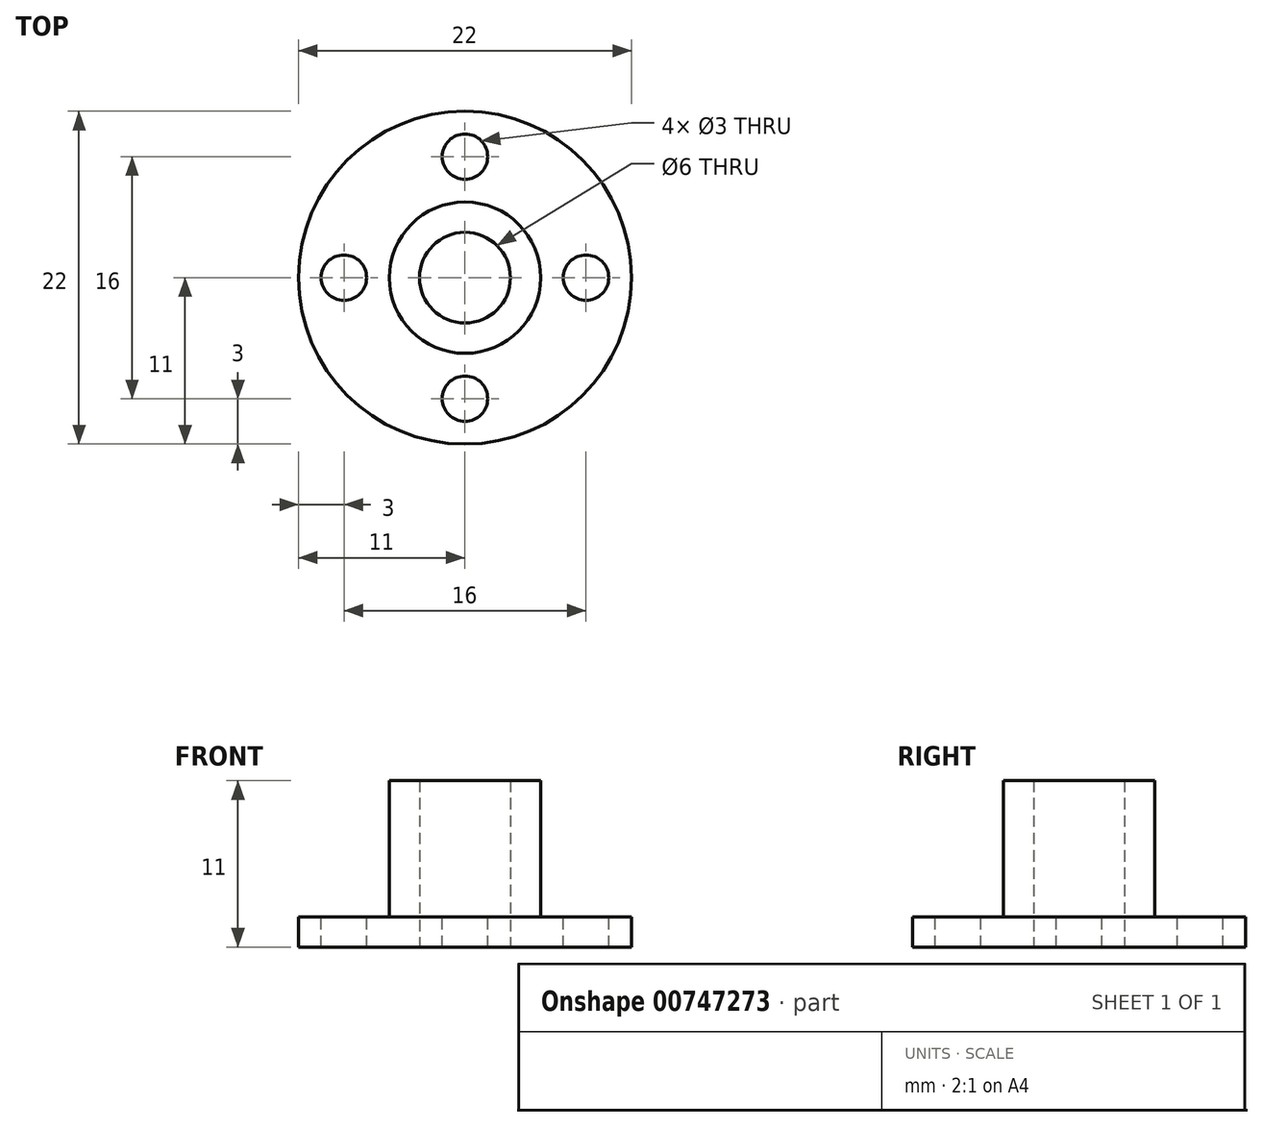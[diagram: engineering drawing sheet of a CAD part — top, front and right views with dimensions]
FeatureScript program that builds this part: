
annotation { "Feature Type Name" : "Feature", "Feature Type Description" : "" }
export const myFeature = defineFeature(function(context is Context, id is Id, definition is map)
    precondition{}
    {
        {
            var Q0;
            Q0=qCreatedBy(makeId("Top.planeOp"),FACE);
            var sketch = newSketch(context, id + "F0", { "sketchPlane" : qUnion([Q0])});
            skCircle(sketch, "E0", {"center": v(0, 0) * mm, "radius": 11 * mm});
            skSolve(sketch);
        }
        {
            var Q0;
            Q0=qSketchRegion(id+"F0",true);
            extrude(context, id + "F1", {"entities" : qUnion([Q0]), "depth" : 2 * mm, "offsetDistance" : 25 * mm});
        }
        {
            var Q0;
            Q0=makeQuery(id+"F1.opExtrude","CAP_FACE",FACE,{"disambiguationData":[OSD([sQuery(id+"F0.wireOp",EDGE,"E0")])],"isStart":false});
            var sketch = newSketch(context, id + "F2", { "sketchPlane" : qUnion([Q0])});
            skCircle(sketch, "E1", {"center": v(0, 0) * mm, "radius": 5 * mm});
            skCircle(sketch, "E2", {"center": v(0, 0) * mm, "radius": 3 * mm});
            skSolve(sketch);
        }
        {
            var Q0;
            Q0=makeQuery(id+"F2.imprint","IMPRINT",FACE,{"disambiguationData":[TD([[makeQuery(id+"F2.imprint","IMPRINT",EDGE,{"derivedFrom":sQuery(id+"F2.wireOp",EDGE,"E1")}),1.0]])]});
            extrude(context, id + "F3", {"entities" : qUnion([Q0]), "operationType" : NewBodyOperationType.ADD, "depth" : 9 * mm, "offsetDistance" : 25 * mm});
        }
        {
            var Q0;
            Q0=makeQuery(id+"F3.boolean.opBoolean","SPLIT",FACE,{"disambiguationData":[TD([makeQuery(id+"F3.opExtrude","SWEPT_FACE",FACE,{"disambiguationData":[OSD([sQuery(id+"F2.wireOp",EDGE,"E2")])]})])],"derivedFrom":makeQuery(id+"F1.opExtrude","CAP_FACE",FACE,{"disambiguationData":[OSD([sQuery(id+"F0.wireOp",EDGE,"E0")])],"isStart":false})});
            var sketch = newSketch(context, id + "F4", { "sketchPlane" : qUnion([Q0])});
            skCircle(sketch, "E3", {"center": v(0, 0) * mm, "radius": 3 * mm});
            skSolve(sketch);
        }
        {
            var Q0;
            Q0=qSketchRegion(id+"F4",true);
            var Q1;
            Q1=makeQuery(id+"F1.opExtrude","CAP_FACE",FACE,{"disambiguationData":[OSD([sQuery(id+"F0.wireOp",EDGE,"E0")])],"isStart":true});
            extrude(context, id + "F5", {"entities" : qUnion([Q0]), "operationType" : NewBodyOperationType.REMOVE, "endBound" : BoundingType.UP_TO_SURFACE, "oppositeDirection" : true, "depth" : 25 * mm, "endBoundEntityFace" : qUnion([Q1]), "offsetDistance" : 25 * mm});
        }
        {
            var Q0;
            {var subQ0=sQuery(id+"F0.wireOp",EDGE,"E0");Q0=makeQuery(id+"F3.boolean.opBoolean","SPLIT",FACE,{"disambiguationData":[TD([makeQuery(id+"F1.opExtrude","SWEPT_FACE",FACE,{"disambiguationData":[OSD([subQ0])]})])],"derivedFrom":makeQuery(id+"F1.opExtrude","CAP_FACE",FACE,{"disambiguationData":[OSD([subQ0])],"isStart":false})});}
            var sketch = newSketch(context, id + "F6", { "sketchPlane" : qUnion([Q0])});
            skCircle(sketch, "E4", {"center": v(0, 0) * mm, "radius": 8 * mm, "construction": true});
            skLineSegment(sketch, "E5", {"start": v(-8, 0) * mm, "end": v(8, 0) * mm, "construction": true});
            skLineSegment(sketch, "E6", {"start": v(0, 8) * mm, "end": v(0, -8) * mm, "construction": true});
            skSolve(sketch);
        }
        {
            var Q0;
            Q0=sQuery(id+"F6.wireOp",VERTEX,"E6.start");
            var Q1;
            Q1=sQuery(id+"F6.wireOp",VERTEX,"E5.end");
            var Q2;
            Q2=sQuery(id+"F6.wireOp",VERTEX,"E6.end");
            var Q3;
            Q3=sQuery(id+"F6.wireOp",VERTEX,"E5.start");
            var Q4;
            Q4=makeQuery(id+"F1.opExtrude","SWEPT_BODY",BODY,{"disambiguationData":[OSD([sQuery(id+"F0.wireOp",EDGE,"E0")])]});
            hole(context, id + "F7", {"style" : HoleStyle.SIMPLE, "endStyle" : HoleEndStyle.THROUGH, "holeDiameter" : 3 * mm, "majorDiameter" : 5 * mm, "isTappedThrough" : true, "tappedDepth" : 12 * mm, "tapClearance" : 3, "locations" : qUnion([Q0, Q1, Q2, Q3]), "scope" : qUnion([Q4])});
        }
    });
